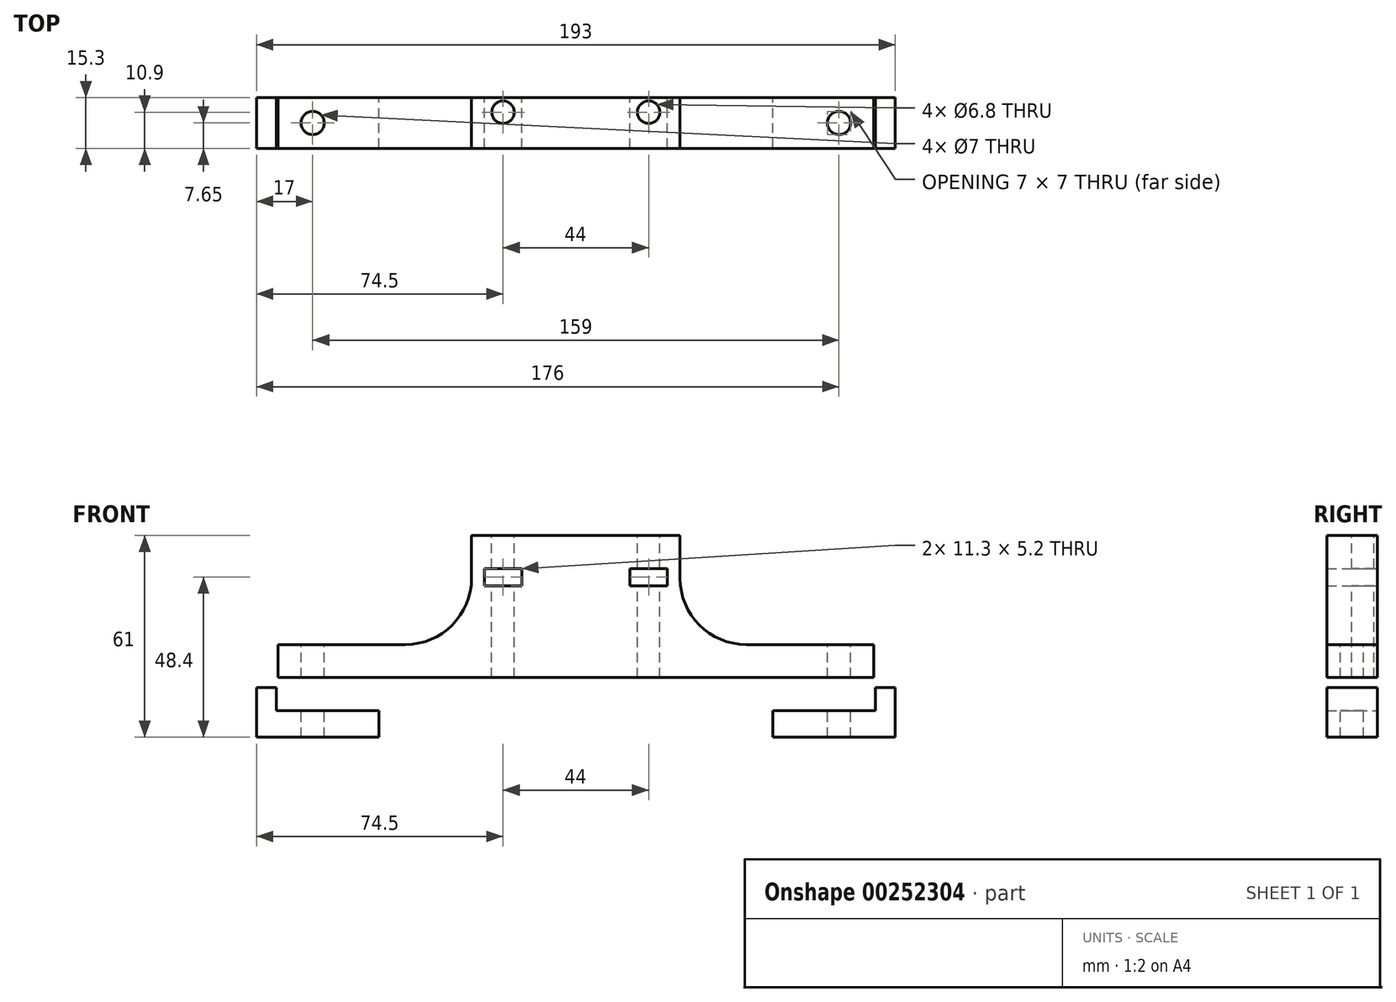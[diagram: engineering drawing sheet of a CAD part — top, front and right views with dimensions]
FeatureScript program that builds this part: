
annotation { "Feature Type Name" : "Feature", "Feature Type Description" : "" }
export const myFeature = defineFeature(function(context is Context, id is Id, definition is map)
    precondition{}
    {
        {
            var Q0;
            Q0=qCreatedBy(makeId("Front.planeOp"),FACE);
            var sketch = newSketch(context, id + "F0", { "sketchPlane" : qUnion([Q0])});
            skLineSegment(sketch, "E0.bottom", {"start": v(-31.5, 0) * mm, "end": v(31.5, 0) * mm});
            skLineSegment(sketch, "E0.top", {"start": v(-31.5, 43) * mm, "end": v(31.5, 43) * mm});
            skLineSegment(sketch, "E0.left", {"start": v(-31.5, 10) * mm, "end": v(-31.5, 43) * mm});
            skLineSegment(sketch, "E0.right", {"start": v(31.5, 10) * mm, "end": v(31.5, 43) * mm});
            skLineSegment(sketch, "E1.bottom", {"start": v(-31.5, 10) * mm, "end": v(-90, 10) * mm});
            skLineSegment(sketch, "E1.top", {"start": v(-31.5, 0) * mm, "end": v(-90, 0) * mm});
            skLineSegment(sketch, "E1.right", {"start": v(-90, 10) * mm, "end": v(-90, 0) * mm});
            skLineSegment(sketch, "E2.bottom", {"start": v(31.5, 10) * mm, "end": v(90, 10) * mm});
            skLineSegment(sketch, "E2.top", {"start": v(31.5, 0) * mm, "end": v(90, 0) * mm});
            skLineSegment(sketch, "E2.right", {"start": v(90, 10) * mm, "end": v(90, 0) * mm});
            skLineSegment(sketch, "E3.bottom", {"start": v(-16.35, 27.8) * mm, "end": v(-27.65, 27.8) * mm});
            skLineSegment(sketch, "E3.top", {"start": v(-16.35, 33) * mm, "end": v(-27.65, 33) * mm});
            skLineSegment(sketch, "E3.left", {"start": v(-16.35, 27.8) * mm, "end": v(-16.35, 33) * mm});
            skLineSegment(sketch, "E3.right", {"start": v(-27.65, 27.8) * mm, "end": v(-27.65, 33) * mm});
            skPoint(sketch, "E3.middle", {"position": v(-22, 30.4) * mm});
            skLineSegment(sketch, "E4", {"start": v(0, 47.48) * mm, "end": v(0, -4.5) * mm, "construction": true});
            skPoint(sketch, "E5.MirrorP", {"position": v(22, 30.4) * mm});
            skLineSegment(sketch, "E6.MirrorCS", {"start": v(27.65, 27.8) * mm, "end": v(27.65, 33) * mm});
            skLineSegment(sketch, "E7.MirrorCS", {"start": v(16.35, 27.8) * mm, "end": v(16.35, 33) * mm});
            skLineSegment(sketch, "E8.MirrorCS", {"start": v(16.35, 33) * mm, "end": v(27.65, 33) * mm});
            skLineSegment(sketch, "E9.MirrorCS", {"start": v(16.35, 27.8) * mm, "end": v(27.65, 27.8) * mm});
            skLineSegment(sketch, "E10.bottom", {"start": v(-96.5, -3) * mm, "end": v(-90.5, -3) * mm});
            skLineSegment(sketch, "E10.right", {"start": v(-90.5, -3) * mm, "end": v(-90.5, -10) * mm});
            skLineSegment(sketch, "E11.bottom", {"start": v(-90.5, -10) * mm, "end": v(-59.5, -10) * mm});
            skLineSegment(sketch, "E11.right", {"start": v(-59.5, -10) * mm, "end": v(-59.5, -18) * mm});
            skLineSegment(sketch, "E12", {"start": v(-96.5, -3) * mm, "end": v(-96.5, -18) * mm});
            skLineSegment(sketch, "E13", {"start": v(-67.5, 10) * mm, "end": v(-67.5, 0) * mm, "construction": true});
            skLineSegment(sketch, "E14", {"start": v(67.5, 10) * mm, "end": v(67.5, 0) * mm, "construction": true});
            skLineSegment(sketch, "E15", {"start": v(-96.5, -18) * mm, "end": v(-59.5, -18) * mm});
            skLineSegment(sketch, "E16.MirrorCS", {"start": v(96.5, -18) * mm, "end": v(59.5, -18) * mm});
            skLineSegment(sketch, "E17.MirrorCS", {"start": v(90.5, -10) * mm, "end": v(59.5, -10) * mm});
            skLineSegment(sketch, "E18.MirrorCS", {"start": v(90.5, -3) * mm, "end": v(90.5, -10) * mm});
            skLineSegment(sketch, "E19.MirrorCS", {"start": v(59.5, -10) * mm, "end": v(59.5, -18) * mm});
            skLineSegment(sketch, "E20.MirrorCS", {"start": v(96.5, -3) * mm, "end": v(96.5, -18) * mm});
            skLineSegment(sketch, "E21.MirrorCS", {"start": v(96.5, -3) * mm, "end": v(90.5, -3) * mm});
            skSolve(sketch);
        }
        {
            var Q0;
            Q0 = qSketchRegion(id + "F0", true);
            extrude(context, id + "F1", {"entities" : qUnion([Q0]), "endBound" : BoundingType.SYMMETRIC, "depth" : 15.3 * mm});
        }
        {
            var Q0;
            Q0=makeQuery(id+"F1.opExtrude","SWEPT_FACE",FACE,{"disambiguationData":[OSD([sQuery(id+"F0.wireOp",EDGE,"E0.top")])]});
            var sketch = newSketch(context, id + "F2", { "sketchPlane" : qUnion([Q0])});
            skCircle(sketch, "E22", {"center": v(-22, 3.25) * mm, "radius": 3.4 * mm});
            skPoint(sketch, "E22.centerSnap0", {"position": v(-31.5, 0) * mm});
            skLineSegment(sketch, "E23", {"start": v(0, 21.5) * mm, "end": v(0, -35.16) * mm, "construction": true});
            skCircle(sketch, "E24.MirrorC", {"center": v(22, 3.25) * mm, "radius": 3.4 * mm});
            skSolve(sketch);
        }
        {
            var Q0;
            Q0 = qSketchRegion(id + "F2", true);
            var Q1;
            Q1=makeQuery(id+"F1.opExtrude","SWEPT_FACE",FACE,{"disambiguationData":[OSD([sQuery(id+"F0.wireOp",EDGE,"E0.bottom"),sQuery(id+"F0.wireOp",EDGE,"E1.top"),sQuery(id+"F0.wireOp",EDGE,"E2.top")])]});
            extrude(context, id + "F3", {"entities" : qUnion([Q0]), "operationType" : NewBodyOperationType.REMOVE, "endBound" : BoundingType.UP_TO_SURFACE, "oppositeDirection" : true, "endBoundEntityFace" : qUnion([Q1]), "depth" : 25 * mm});
        }
        {
            var Q0;
            Q0=makeQuery(id+"F1.opExtrude","SWEPT_FACE",FACE,{"disambiguationData":[OSD([sQuery(id+"F0.wireOp",EDGE,"E1.bottom")])]});
            var sketch = newSketch(context, id + "F4", { "sketchPlane" : qUnion([Q0])});
            skCircle(sketch, "E25", {"center": v(-79.5, 0) * mm, "radius": 3.5 * mm});
            skPoint(sketch, "E25.centerSnap0", {"position": v(-90, 0) * mm});
            skLineSegment(sketch, "E26", {"start": v(0, 38.65) * mm, "end": v(0, -45.04) * mm, "construction": true});
            skCircle(sketch, "E27.MirrorC", {"center": v(79.5, 0) * mm, "radius": 3.5 * mm});
            skSolve(sketch);
        }
        {
            var Q0;
            Q0 = qSketchRegion(id + "F4", true);
            var Q1;
            Q1=makeQuery(id+"F1.opExtrude","SWEPT_FACE",FACE,{"disambiguationData":[OSD([sQuery(id+"F0.wireOp",EDGE,"E15")])]});
            extrude(context, id + "F5", {"entities" : qUnion([Q0]), "operationType" : NewBodyOperationType.REMOVE, "endBound" : BoundingType.UP_TO_SURFACE, "oppositeDirection" : true, "endBoundEntityFace" : qUnion([Q1]), "depth" : 25 * mm});
        }
        {
            var Q0;
            Q0=makeQuery(id+"F1.opExtrude","SWEPT_EDGE",EDGE,{"disambiguationData":[OSD([sQuery(id+"F0.wireOp",EDGE,"E0.right"),sQuery(id+"F0.wireOp",EDGE,"E2.bottom")])]});
            var Q1;
            Q1=makeQuery(id+"F1.opExtrude","SWEPT_EDGE",EDGE,{"disambiguationData":[OSD([sQuery(id+"F0.wireOp",EDGE,"E0.left"),sQuery(id+"F0.wireOp",EDGE,"E1.bottom")])]});
            fillet(context, id + "F6", {"entities" : qUnion([Q0, Q1]), "radius" : 20 * mm, "tangentPropagation" : true, "allowEdgeOverflow" : false});
        }
    });
